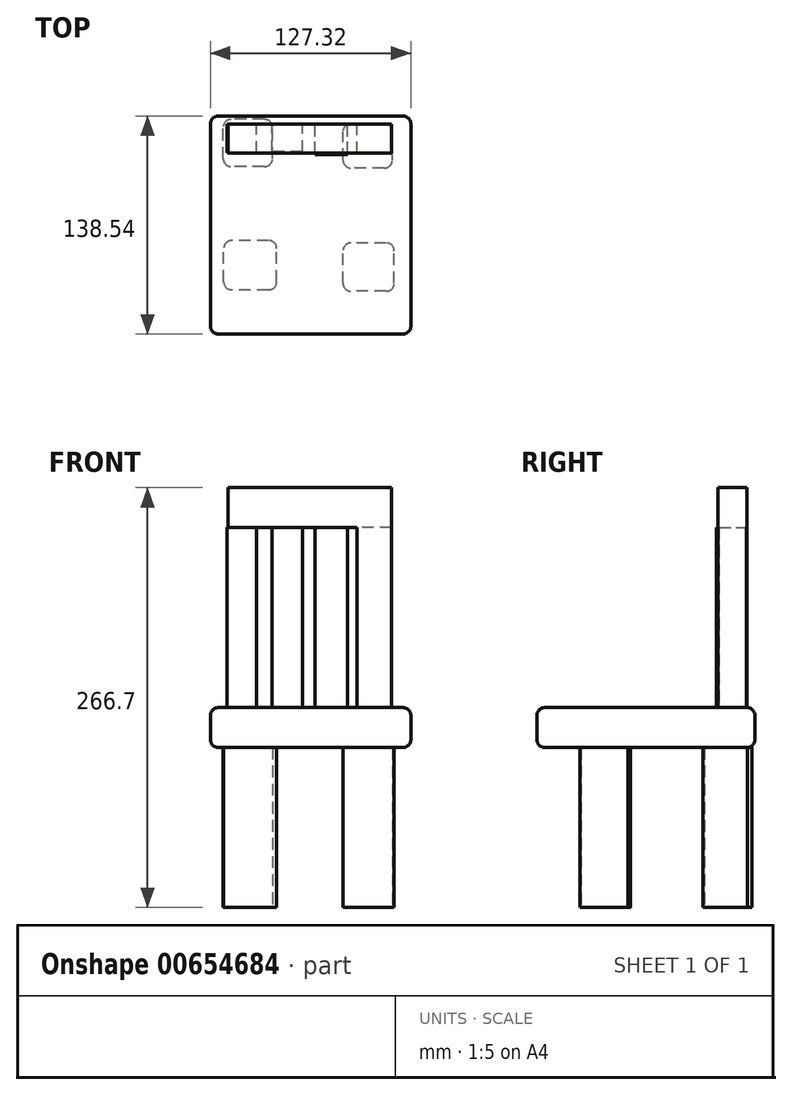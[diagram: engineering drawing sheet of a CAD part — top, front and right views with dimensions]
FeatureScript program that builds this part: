
annotation { "Feature Type Name" : "Feature", "Feature Type Description" : "" }
export const myFeature = defineFeature(function(context is Context, id is Id, definition is map)
    precondition{}
    {
        {
            var Q0;
            Q0=qCreatedBy(makeId("Top.planeOp"),FACE);
            var sketch = newSketch(context, id + "F0", { "sketchPlane" : qUnion([Q0])});
            skLineSegment(sketch, "E0.bottom", {"start": v(-24.21, 23.91) * mm, "end": v(-55.5, 23.91) * mm});
            skLineSegment(sketch, "E0.top", {"start": v(-24.21, 54) * mm, "end": v(-55.5, 54) * mm});
            skLineSegment(sketch, "E0.left", {"start": v(-24.21, 23.91) * mm, "end": v(-24.21, 54) * mm});
            skLineSegment(sketch, "E0.right", {"start": v(-55.5, 23.91) * mm, "end": v(-55.5, 54) * mm});
            skPoint(sketch, "E0.middle", {"position": v(-39.85, 38.95) * mm});
            skLineSegment(sketch, "E1.bottom", {"start": v(51.89, 23.01) * mm, "end": v(20.6, 23.01) * mm});
            skLineSegment(sketch, "E1.top", {"start": v(51.89, 51.28) * mm, "end": v(20.6, 51.28) * mm});
            skLineSegment(sketch, "E1.left", {"start": v(51.89, 23.01) * mm, "end": v(51.89, 51.28) * mm});
            skLineSegment(sketch, "E1.right", {"start": v(20.6, 23.01) * mm, "end": v(20.6, 51.28) * mm});
            skPoint(sketch, "E1.middle", {"position": v(36.25, 37.15) * mm});
            skLineSegment(sketch, "E2.bottom", {"start": v(-21.5, -54.3) * mm, "end": v(-55.2, -54.3) * mm});
            skLineSegment(sketch, "E2.top", {"start": v(-21.5, -23.01) * mm, "end": v(-55.2, -23.01) * mm});
            skLineSegment(sketch, "E2.left", {"start": v(-21.5, -54.3) * mm, "end": v(-21.5, -23.01) * mm});
            skLineSegment(sketch, "E2.right", {"start": v(-55.2, -54.3) * mm, "end": v(-55.2, -23.01) * mm});
            skPoint(sketch, "E2.middle", {"position": v(-38.35, -38.65) * mm});
            skLineSegment(sketch, "E3.bottom", {"start": v(53.09, -55.2) * mm, "end": v(20.6, -55.2) * mm});
            skLineSegment(sketch, "E3.top", {"start": v(53.09, -24.51) * mm, "end": v(20.6, -24.51) * mm});
            skLineSegment(sketch, "E3.left", {"start": v(53.09, -55.2) * mm, "end": v(53.09, -24.51) * mm});
            skLineSegment(sketch, "E3.right", {"start": v(20.6, -55.2) * mm, "end": v(20.6, -24.51) * mm});
            skPoint(sketch, "E3.middle", {"position": v(36.85, -39.85) * mm});
            skSolve(sketch);
        }
        {
            var Q0;
            Q0 = qSketchRegion(id + "F0", true);
            extrude(context, id + "F1", {"entities" : qUnion([Q0]), "depth" : 101.6 * mm, "offsetDistance" : 25.4 * mm});
        }
        {
            var Q0;
            Q0=makeQuery(id+"F1.opExtrude","CAP_FACE",FACE,{"disambiguationData":[OSD([sQuery(id+"F0.wireOp",EDGE,"E2.bottom"),sQuery(id+"F0.wireOp",EDGE,"E2.top"),sQuery(id+"F0.wireOp",EDGE,"E2.left"),sQuery(id+"F0.wireOp",EDGE,"E2.right")])],"isStart":false});
            var sketch = newSketch(context, id + "F2", { "sketchPlane" : qUnion([Q0])});
            skLineSegment(sketch, "E4.bottom", {"start": v(-63.62, 56.1) * mm, "end": v(63.7, 56.1) * mm});
            skLineSegment(sketch, "E4.top", {"start": v(-63.62, -82.44) * mm, "end": v(63.7, -82.44) * mm});
            skLineSegment(sketch, "E4.left", {"start": v(-63.62, 56.1) * mm, "end": v(-63.62, -82.44) * mm});
            skLineSegment(sketch, "E4.right", {"start": v(63.7, 56.1) * mm, "end": v(63.7, -82.44) * mm});
            skSolve(sketch);
        }
        {
            var Q0;
            Q0 = qSketchRegion(id + "F2", true);
            extrude(context, id + "F3", {"entities" : qUnion([Q0]), "depth" : 25.4 * mm, "offsetDistance" : 25.4 * mm});
        }
        {
            var Q0;
            Q0=makeQuery(id+"F3.opExtrude","SWEPT_FACE",FACE,{"disambiguationData":[OSD([sQuery(id+"F2.wireOp",EDGE,"E4.top")])]});
            var Q1;
            Q1=makeQuery(id+"F3.opExtrude","SWEPT_FACE",FACE,{"disambiguationData":[OSD([sQuery(id+"F2.wireOp",EDGE,"E4.left")])]});
            var Q2;
            Q2=makeQuery(id+"F3.opExtrude","SWEPT_FACE",FACE,{"disambiguationData":[OSD([sQuery(id+"F2.wireOp",EDGE,"E4.right")])]});
            var Q3;
            Q3=makeQuery(id+"F3.opExtrude","SWEPT_FACE",FACE,{"disambiguationData":[OSD([sQuery(id+"F2.wireOp",EDGE,"E4.bottom")])]});
            fillet(context, id + "F4", {"entities" : qUnion([Q0, Q1, Q2, Q3]), "radius" : 5.08 * mm, "tangentPropagation" : true, "allowEdgeOverflow" : false});
        }
        {
            var Q0;
            Q0=makeQuery(id+"F3.opExtrude","CAP_FACE",FACE,{"disambiguationData":[OSD([sQuery(id+"F2.wireOp",EDGE,"E4.bottom"),sQuery(id+"F2.wireOp",EDGE,"E4.top"),sQuery(id+"F2.wireOp",EDGE,"E4.left"),sQuery(id+"F2.wireOp",EDGE,"E4.right")])],"isStart":false});
            var sketch = newSketch(context, id + "F5", { "sketchPlane" : qUnion([Q0])});
            skLineSegment(sketch, "E5.bottom", {"start": v(-34.29, 32.73) * mm, "end": v(-53.07, 32.73) * mm});
            skLineSegment(sketch, "E5.top", {"start": v(-34.29, 50.9) * mm, "end": v(-53.07, 50.9) * mm});
            skLineSegment(sketch, "E5.left", {"start": v(-34.29, 32.73) * mm, "end": v(-34.29, 50.9) * mm});
            skLineSegment(sketch, "E5.right", {"start": v(-53.07, 32.73) * mm, "end": v(-53.07, 50.9) * mm});
            skPoint(sketch, "E5.middle", {"position": v(-43.68, 41.81) * mm});
            skLineSegment(sketch, "E6.bottom", {"start": v(-5.17, 33.36) * mm, "end": v(-24.58, 33.36) * mm});
            skLineSegment(sketch, "E6.top", {"start": v(-5.17, 50.9) * mm, "end": v(-24.58, 50.9) * mm});
            skLineSegment(sketch, "E6.left", {"start": v(-5.17, 33.36) * mm, "end": v(-5.17, 50.9) * mm});
            skLineSegment(sketch, "E6.right", {"start": v(-24.58, 33.36) * mm, "end": v(-24.58, 50.9) * mm});
            skPoint(sketch, "E6.middle", {"position": v(-14.87, 42.12) * mm});
            skLineSegment(sketch, "E7.bottom", {"start": v(23.33, 31.48) * mm, "end": v(2.66, 31.48) * mm});
            skLineSegment(sketch, "E7.top", {"start": v(23.33, 50.26) * mm, "end": v(2.66, 50.26) * mm});
            skLineSegment(sketch, "E7.left", {"start": v(23.33, 31.48) * mm, "end": v(23.33, 50.26) * mm});
            skLineSegment(sketch, "E7.right", {"start": v(2.66, 31.48) * mm, "end": v(2.66, 50.26) * mm});
            skPoint(sketch, "E7.middle", {"position": v(13, 40.87) * mm});
            skLineSegment(sketch, "E8.bottom", {"start": v(51.5, 32.42) * mm, "end": v(29.59, 32.42) * mm});
            skLineSegment(sketch, "E8.top", {"start": v(51.5, 50.58) * mm, "end": v(29.59, 50.58) * mm});
            skLineSegment(sketch, "E8.left", {"start": v(51.5, 32.42) * mm, "end": v(51.5, 50.58) * mm});
            skLineSegment(sketch, "E8.right", {"start": v(29.59, 32.42) * mm, "end": v(29.59, 50.58) * mm});
            skPoint(sketch, "E8.middle", {"position": v(40.55, 41.5) * mm});
            skSolve(sketch);
        }
        {
            var Q0;
            Q0=makeQuery(id+"F5.imprint","IMPRINT",FACE,{"disambiguationData":[TD([[makeQuery(id+"F5.imprint","IMPRINT",EDGE,{"derivedFrom":sQuery(id+"F5.wireOp",EDGE,"E5.bottom")}),-1.0]])]});
            var Q1;
            Q1=makeQuery(id+"F5.imprint","IMPRINT",FACE,{"disambiguationData":[TD([[makeQuery(id+"F5.imprint","IMPRINT",EDGE,{"derivedFrom":sQuery(id+"F5.wireOp",EDGE,"E6.bottom")}),-1.0]])]});
            var Q2;
            Q2=makeQuery(id+"F5.imprint","IMPRINT",FACE,{"disambiguationData":[TD([[makeQuery(id+"F5.imprint","IMPRINT",EDGE,{"derivedFrom":sQuery(id+"F5.wireOp",EDGE,"E7.bottom")}),-1.0]])]});
            var Q3;
            Q3=makeQuery(id+"F5.imprint","IMPRINT",FACE,{"disambiguationData":[TD([[makeQuery(id+"F5.imprint","IMPRINT",EDGE,{"derivedFrom":sQuery(id+"F5.wireOp",EDGE,"E8.bottom")}),-1.0]])]});
            extrude(context, id + "F6", {"entities" : qUnion([Q0, Q1, Q2, Q3]), "operationType" : NewBodyOperationType.ADD, "depth" : 114.3 * mm, "offsetDistance" : 25.4 * mm});
        }
        {
            var Q0;
            Q0=makeQuery(id+"F6.opExtrude","CAP_FACE",FACE,{"disambiguationData":[OSD([sQuery(id+"F5.wireOp",EDGE,"E6.bottom"),sQuery(id+"F5.wireOp",EDGE,"E6.top"),sQuery(id+"F5.wireOp",EDGE,"E6.left"),sQuery(id+"F5.wireOp",EDGE,"E6.right")])],"isStart":false});
            var sketch = newSketch(context, id + "F7", { "sketchPlane" : qUnion([Q0])});
            skLineSegment(sketch, "E9.bottom", {"start": v(-52.45, 50.9) * mm, "end": v(51.5, 50.9) * mm});
            skLineSegment(sketch, "E9.top", {"start": v(-52.45, 32.42) * mm, "end": v(51.5, 32.42) * mm});
            skLineSegment(sketch, "E9.left", {"start": v(-52.45, 50.9) * mm, "end": v(-52.45, 32.42) * mm});
            skLineSegment(sketch, "E9.right", {"start": v(51.5, 50.9) * mm, "end": v(51.5, 32.42) * mm});
            skSolve(sketch);
        }
        {
            var Q0;
            Q0 = qSketchRegion(id + "F7", true);
            extrude(context, id + "F8", {"entities" : qUnion([Q0]), "operationType" : NewBodyOperationType.ADD, "depth" : 25.4 * mm, "offsetDistance" : 25.4 * mm});
        }
        {
            var Q0;
            Q0=makeQuery(id+"F1.opExtrude","SWEPT_EDGE",EDGE,{"disambiguationData":[OSD([sQuery(id+"F0.wireOp",EDGE,"E3.bottom"),sQuery(id+"F0.wireOp",EDGE,"E3.left")])]});
            var Q1;
            Q1=makeQuery(id+"F1.opExtrude","SWEPT_EDGE",EDGE,{"disambiguationData":[OSD([sQuery(id+"F0.wireOp",EDGE,"E3.top"),sQuery(id+"F0.wireOp",EDGE,"E3.left")])]});
            var Q2;
            Q2=makeQuery(id+"F1.opExtrude","SWEPT_EDGE",EDGE,{"disambiguationData":[OSD([sQuery(id+"F0.wireOp",EDGE,"E3.top"),sQuery(id+"F0.wireOp",EDGE,"E3.right")])]});
            var Q3;
            Q3=makeQuery(id+"F1.opExtrude","SWEPT_EDGE",EDGE,{"disambiguationData":[OSD([sQuery(id+"F0.wireOp",EDGE,"E3.bottom"),sQuery(id+"F0.wireOp",EDGE,"E3.right")])]});
            fillet(context, id + "F9", {"entities" : qUnion([Q0, Q1, Q2, Q3]), "radius" : 5.08 * mm, "tangentPropagation" : true, "allowEdgeOverflow" : false});
        }
        {
            var Q0;
            Q0=makeQuery(id+"F1.opExtrude","SWEPT_EDGE",EDGE,{"disambiguationData":[OSD([sQuery(id+"F0.wireOp",EDGE,"E2.bottom"),sQuery(id+"F0.wireOp",EDGE,"E2.right")])]});
            var Q1;
            Q1=makeQuery(id+"F1.opExtrude","SWEPT_EDGE",EDGE,{"disambiguationData":[OSD([sQuery(id+"F0.wireOp",EDGE,"E2.top"),sQuery(id+"F0.wireOp",EDGE,"E2.right")])]});
            var Q2;
            Q2=makeQuery(id+"F1.opExtrude","SWEPT_EDGE",EDGE,{"disambiguationData":[OSD([sQuery(id+"F0.wireOp",EDGE,"E2.bottom"),sQuery(id+"F0.wireOp",EDGE,"E2.left")])]});
            var Q3;
            Q3=makeQuery(id+"F1.opExtrude","SWEPT_EDGE",EDGE,{"disambiguationData":[OSD([sQuery(id+"F0.wireOp",EDGE,"E2.top"),sQuery(id+"F0.wireOp",EDGE,"E2.left")])]});
            fillet(context, id + "F10", {"entities" : qUnion([Q0, Q1, Q2, Q3]), "radius" : 5.08 * mm, "tangentPropagation" : true, "allowEdgeOverflow" : false});
        }
        {
            var Q0;
            Q0=makeQuery(id+"F1.opExtrude","SWEPT_EDGE",EDGE,{"disambiguationData":[OSD([sQuery(id+"F0.wireOp",EDGE,"E0.top"),sQuery(id+"F0.wireOp",EDGE,"E0.right")])]});
            var Q1;
            Q1=makeQuery(id+"F1.opExtrude","SWEPT_EDGE",EDGE,{"disambiguationData":[OSD([sQuery(id+"F0.wireOp",EDGE,"E0.bottom"),sQuery(id+"F0.wireOp",EDGE,"E0.right")])]});
            var Q2;
            Q2=makeQuery(id+"F1.opExtrude","SWEPT_EDGE",EDGE,{"disambiguationData":[OSD([sQuery(id+"F0.wireOp",EDGE,"E0.top"),sQuery(id+"F0.wireOp",EDGE,"E0.left")])]});
            var Q3;
            Q3=makeQuery(id+"F1.opExtrude","SWEPT_EDGE",EDGE,{"disambiguationData":[OSD([sQuery(id+"F0.wireOp",EDGE,"E0.bottom"),sQuery(id+"F0.wireOp",EDGE,"E0.left")])]});
            fillet(context, id + "F11", {"entities" : qUnion([Q0, Q1, Q2, Q3]), "radius" : 5.08 * mm, "tangentPropagation" : true, "allowEdgeOverflow" : false});
        }
        {
            var Q0;
            Q0=makeQuery(id+"F1.opExtrude","SWEPT_EDGE",EDGE,{"disambiguationData":[OSD([sQuery(id+"F0.wireOp",EDGE,"E1.bottom"),sQuery(id+"F0.wireOp",EDGE,"E1.left")])]});
            var Q1;
            Q1=makeQuery(id+"F1.opExtrude","SWEPT_EDGE",EDGE,{"disambiguationData":[OSD([sQuery(id+"F0.wireOp",EDGE,"E1.top"),sQuery(id+"F0.wireOp",EDGE,"E1.left")])]});
            var Q2;
            Q2=makeQuery(id+"F1.opExtrude","SWEPT_EDGE",EDGE,{"disambiguationData":[OSD([sQuery(id+"F0.wireOp",EDGE,"E1.bottom"),sQuery(id+"F0.wireOp",EDGE,"E1.right")])]});
            var Q3;
            Q3=makeQuery(id+"F1.opExtrude","SWEPT_EDGE",EDGE,{"disambiguationData":[OSD([sQuery(id+"F0.wireOp",EDGE,"E1.top"),sQuery(id+"F0.wireOp",EDGE,"E1.right")])]});
            fillet(context, id + "F12", {"entities" : qUnion([Q0, Q1, Q2, Q3]), "radius" : 5.08 * mm, "tangentPropagation" : true, "allowEdgeOverflow" : false});
        }
    });
